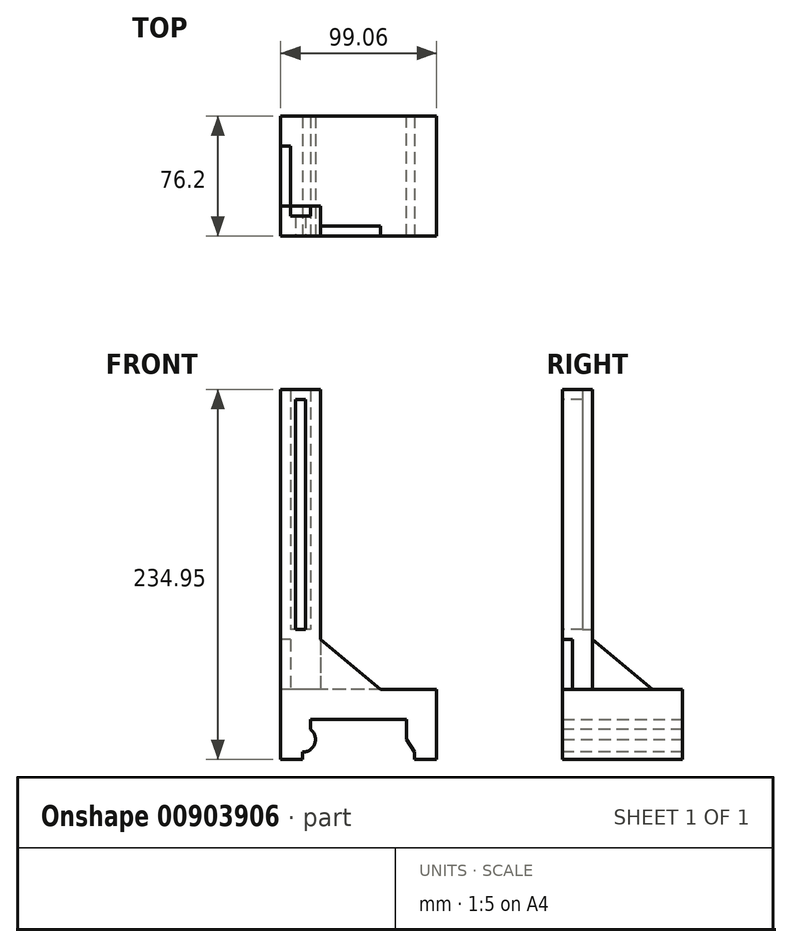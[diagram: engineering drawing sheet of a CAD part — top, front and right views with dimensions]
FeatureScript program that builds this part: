
annotation { "Feature Type Name" : "Feature", "Feature Type Description" : "" }
export const myFeature = defineFeature(function(context is Context, id is Id, definition is map)
    precondition{}
    {
        {
            var Q0;
            Q0=qCreatedBy(makeId("Front.planeOp"),FACE);
            var sketch = newSketch(context, id + "F0", { "sketchPlane" : qUnion([Q0])});
            skLineSegment(sketch, "E0.bottom", {"start": v(49.53, -22.23) * mm, "end": v(-49.53, -22.23) * mm});
            skLineSegment(sketch, "E0.top", {"start": v(49.53, 22.23) * mm, "end": v(-49.53, 22.23) * mm});
            skLineSegment(sketch, "E0.left", {"start": v(49.53, -22.23) * mm, "end": v(49.53, 22.23) * mm});
            skLineSegment(sketch, "E0.right", {"start": v(-49.53, -22.23) * mm, "end": v(-49.53, 22.22) * mm});
            skPoint(sketch, "E0.middle", {"position": v(0, 0) * mm});
            skLineSegment(sketch, "E1.bottom", {"start": v(30.48, -47.63) * mm, "end": v(-30.48, -47.63) * mm});
            skLineSegment(sketch, "E1.top", {"start": v(30.48, 3.18) * mm, "end": v(-30.48, 3.18) * mm});
            skLineSegment(sketch, "E1.left", {"start": v(30.48, -47.63) * mm, "end": v(30.48, 3.18) * mm});
            skLineSegment(sketch, "E1.right", {"start": v(-30.48, -47.63) * mm, "end": v(-30.48, 3.18) * mm});
            skPoint(sketch, "E1.middle", {"position": v(0, -22.23) * mm});
            skSolve(sketch);
        }
        {
            var Q0;
            Q0=makeQuery(id+"F0.imprint","IMPRINT",FACE,{"disambiguationData":[TD([[makeQuery(id+"F0.imprint","IMPRINT",EDGE,{"derivedFrom":sQuery(id+"F0.wireOp",EDGE,"E0.top")}),1.0]])]});
            extrude(context, id + "F1", {"entities" : qUnion([Q0]), "endBound" : BoundingType.SYMMETRIC, "depth" : 76.2 * mm, "offsetDistance" : 25.4 * mm});
        }
        {
            var Q0;
            Q0=qCreatedBy(makeId("Front.planeOp"),FACE);
            var sketch = newSketch(context, id + "F2", { "sketchPlane" : qUnion([Q0])});
            skLineSegment(sketch, "E2.bottom", {"start": v(35.56, -36.92) * mm, "end": v(-35.56, -36.92) * mm});
            skLineSegment(sketch, "E2.top", {"start": v(35.56, -9.52) * mm, "end": v(-35.56, -9.53) * mm});
            skLineSegment(sketch, "E2.left", {"start": v(35.56, -36.92) * mm, "end": v(35.56, -9.53) * mm});
            skLineSegment(sketch, "E2.right", {"start": v(-35.56, -36.92) * mm, "end": v(-35.56, -9.53) * mm});
            skPoint(sketch, "E2.middle", {"position": v(0, -23.22) * mm});
            skSolve(sketch);
        }
        {
            var Q0;
            Q0=makeQuery(id+"F2.imprint","IMPRINT",FACE,{"disambiguationData":[TD([[makeQuery(id+"F2.imprint","IMPRINT",EDGE,{"derivedFrom":sQuery(id+"F2.wireOp",EDGE,"E2.bottom")}),-1.0]])]});
            extrude(context, id + "F3", {"entities" : qUnion([Q0]), "operationType" : NewBodyOperationType.REMOVE, "endBound" : BoundingType.SYMMETRIC, "oppositeDirection" : true, "depth" : 101.6 * mm, "offsetDistance" : 25.4 * mm});
        }
        {
            var Q0;
            Q0=makeQuery(id+"F1.opExtrude","SWEPT_FACE",FACE,{"disambiguationData":[OSD([sQuery(id+"F0.wireOp",EDGE,"E0.top")])]});
            var sketch = newSketch(context, id + "F4", { "sketchPlane" : qUnion([Q0])});
            skPoint(sketch, "E3.right.end.orphan", {"position": v(-7.9, -5.96) * mm});
            skPoint(sketch, "E3.bottom.end.orphan", {"position": v(-7.9, -51.19) * mm});
            skLineSegment(sketch, "E4.bottom", {"start": v(-24.13, -38.1) * mm, "end": v(-49.53, -38.1) * mm});
            skLineSegment(sketch, "E4.top", {"start": v(-24.13, -19.05) * mm, "end": v(-49.53, -19.05) * mm});
            skLineSegment(sketch, "E4.left", {"start": v(-24.13, -38.1) * mm, "end": v(-24.13, -19.05) * mm});
            skLineSegment(sketch, "E4.right", {"start": v(-49.53, -38.1) * mm, "end": v(-49.53, -19.05) * mm});
            skPoint(sketch, "E4.middle", {"position": v(-36.83, -28.58) * mm});
            skSolve(sketch);
        }
        {
            var Q0;
            Q0=qSketchRegion(id+"F4",true);
            extrude(context, id + "F5", {"entities" : qUnion([Q0]), "operationType" : NewBodyOperationType.ADD, "depth" : 190.5 * mm, "offsetDistance" : 25.4 * mm});
        }
        {
            var Q0;
            Q0=makeQuery(id+"F5.opExtrude","SWEPT_FACE",FACE,{"disambiguationData":[OSD([sQuery(id+"F4.wireOp",EDGE,"E4.top")])]});
            var sketch = newSketch(context, id + "F6", { "sketchPlane" : qUnion([Q0])});
            skLineSegment(sketch, "E5.bottom", {"start": v(30.48, 212.73) * mm, "end": v(43.18, 212.73) * mm});
            skLineSegment(sketch, "E5.top", {"start": v(30.48, 60.33) * mm, "end": v(43.18, 60.33) * mm});
            skLineSegment(sketch, "E5.left", {"start": v(30.48, 212.73) * mm, "end": v(30.48, 60.33) * mm});
            skLineSegment(sketch, "E5.right", {"start": v(43.18, 212.73) * mm, "end": v(43.18, 60.33) * mm});
            skPoint(sketch, "E5.middle", {"position": v(36.83, 136.53) * mm});
            skSolve(sketch);
        }
        {
            var Q0;
            Q0=makeQuery(id+"F6.imprint","IMPRINT",FACE,{"disambiguationData":[TD([[makeQuery(id+"F6.imprint","IMPRINT",EDGE,{"derivedFrom":sQuery(id+"F6.wireOp",EDGE,"E5.bottom")}),-1.0]])]});
            extrude(context, id + "F7", {"entities" : qUnion([Q0]), "operationType" : NewBodyOperationType.REMOVE, "oppositeDirection" : true, "depth" : 6.35 * mm, "offsetDistance" : 25.4 * mm});
        }
        {
            var Q0;
            Q0=makeQuery(id+"F5.opExtrude","SWEPT_FACE",FACE,{"disambiguationData":[OSD([sQuery(id+"F4.wireOp",EDGE,"E4.top")])]});
            var sketch = newSketch(context, id + "F8", { "sketchPlane" : qUnion([Q0])});
            skLineSegment(sketch, "E6.bottom", {"start": v(33.65, 225.43) * mm, "end": v(20.96, 225.43) * mm});
            skLineSegment(sketch, "E6.top", {"start": v(33.66, 200.03) * mm, "end": v(20.96, 200.03) * mm});
            skLineSegment(sketch, "E6.left", {"start": v(33.65, 225.43) * mm, "end": v(33.66, 200.03) * mm});
            skLineSegment(sketch, "E6.right", {"start": v(20.96, 225.43) * mm, "end": v(20.96, 200.03) * mm});
            skPoint(sketch, "E6.middle", {"position": v(27.3, 212.73) * mm});
            skSolve(sketch);
        }
        {
            var Q0;
            {var subQ0=sQuery(id+"F8.wireOp",EDGE,"E6.bottom");Q0=makeQuery(id+"F8.imprint","IMPRINT",FACE,{"disambiguationData":[TD([[makeQuery(id+"F8.imprint","IMPRINT",EDGE,{"derivedFrom":subQ0}),1.0]])]});}
            var Q1;
            {var subQ0=sQuery(id+"F8.wireOp",EDGE,"E6.top");Q1=makeQuery(id+"F8.imprint","IMPRINT",FACE,{"disambiguationData":[TD([[makeQuery(id+"F8.imprint","IMPRINT",EDGE,{"derivedFrom":subQ0}),-1.0]])]});}
            var Q2;
            {var subQ1=makeQuery(id+"F7.boolean.opBoolean","COPY",EDGE,{"derivedFrom":makeQuery(id+"F7.opExtrude","CAP_EDGE",EDGE,{"disambiguationData":[OSD([sQuery(id+"F6.wireOp",EDGE,"E5.bottom")])],"isStart":true})});Q2=makeQuery(id+"F8.imprint","IMPRINT",FACE,{"disambiguationData":[TD([[makeQuery(id+"F8.imprint","IMPRINT",EDGE,{"derivedFrom":subQ1}),1.0]])]});}
            extrude(context, id + "F9", {"entities" : qUnion([Q0, Q1, Q2]), "operationType" : NewBodyOperationType.REMOVE, "oppositeDirection" : true, "depth" : 6.35 * mm, "offsetDistance" : 25.4 * mm});
        }
        {
            var Q0;
            Q0=makeQuery(id+"FqtUo2dF14dtISF_1.boolean.opBoolean","MERGE",FACE,{"derivedFrom":[makeQuery(id+"F1.opExtrude","CAP_FACE",FACE,{"disambiguationData":[OSD([sQuery(id+"F0.wireOp",EDGE,"E0.bottom"),sQuery(id+"F0.wireOp",EDGE,"E0.top"),sQuery(id+"F0.wireOp",EDGE,"E0.left"),sQuery(id+"F0.wireOp",EDGE,"E0.right"),sQuery(id+"F0.wireOp",EDGE,"E1.top"),sQuery(id+"F0.wireOp",EDGE,"E1.left"),sQuery(id+"F0.wireOp",EDGE,"E1.right")])],"isStart":false}),makeQuery(id+"FqtUo2dF14dtISF_1.opExtrude","CAP_FACE",FACE,{"disambiguationData":[OSD([sQuery(id+"Fa6pJ2o9r3T1tcu_1.wireOp",EDGE,"9ab49e5e-e781-4880-a481-f387394318e1.bottom"),sQuery(id+"Fa6pJ2o9r3T1tcu_1.wireOp",EDGE,"9ab49e5e-e781-4880-a481-f387394318e1.top"),sQuery(id+"Fa6pJ2o9r3T1tcu_1.wireOp",EDGE,"9ab49e5e-e781-4880-a481-f387394318e1.left"),sQuery(id+"Fa6pJ2o9r3T1tcu_1.wireOp",EDGE,"HMghRU8G-1H3M-OJ5W-wMgI-K1z1DDckNYTP"),sQuery(id+"Fa6pJ2o9r3T1tcu_1.wireOp",EDGE,"0KJWoq3j-ts2y-bZzM-44IR-2JegtjsgD1qJ")])],"isStart":true})]});
            var sketch = newSketch(context, id + "F10", { "sketchPlane" : qUnion([Q0])});
            skCircle(sketch, "E7", {"center": v(-35.56, -9.53) * mm, "radius": 8.06 * mm});
            skSolve(sketch);
        }
        {
            var Q0;
            Q0=qSketchRegion(id+"F10",true);
            extrude(context, id + "F11", {"entities" : qUnion([Q0]), "operationType" : NewBodyOperationType.ADD, "oppositeDirection" : true, "depth" : 76.2 * mm, "offsetDistance" : 25.4 * mm});
        }
        {
            var Q0;
            Q0=makeQuery(id+"F11.boolean.opBoolean","MERGE",FACE,{"derivedFrom":[makeQuery(id+"FqtUo2dF14dtISF_1.boolean.opBoolean","MERGE",FACE,{"derivedFrom":[makeQuery(id+"F1.opExtrude","CAP_FACE",FACE,{"disambiguationData":[OSD([sQuery(id+"F0.wireOp",EDGE,"E0.bottom"),sQuery(id+"F0.wireOp",EDGE,"E0.top"),sQuery(id+"F0.wireOp",EDGE,"E0.left"),sQuery(id+"F0.wireOp",EDGE,"E0.right"),sQuery(id+"F0.wireOp",EDGE,"E1.top"),sQuery(id+"F0.wireOp",EDGE,"E1.left"),sQuery(id+"F0.wireOp",EDGE,"E1.right")])],"isStart":false}),makeQuery(id+"FqtUo2dF14dtISF_1.opExtrude","CAP_FACE",FACE,{"disambiguationData":[OSD([sQuery(id+"Fa6pJ2o9r3T1tcu_1.wireOp",EDGE,"9ab49e5e-e781-4880-a481-f387394318e1.bottom"),sQuery(id+"Fa6pJ2o9r3T1tcu_1.wireOp",EDGE,"9ab49e5e-e781-4880-a481-f387394318e1.top"),sQuery(id+"Fa6pJ2o9r3T1tcu_1.wireOp",EDGE,"9ab49e5e-e781-4880-a481-f387394318e1.left"),sQuery(id+"Fa6pJ2o9r3T1tcu_1.wireOp",EDGE,"HMghRU8G-1H3M-OJ5W-wMgI-K1z1DDckNYTP"),sQuery(id+"Fa6pJ2o9r3T1tcu_1.wireOp",EDGE,"0KJWoq3j-ts2y-bZzM-44IR-2JegtjsgD1qJ")])],"isStart":true})]}),makeQuery(id+"F11.opExtrude","CAP_FACE",FACE,{"disambiguationData":[OSD([sQuery(id+"F10.wireOp",EDGE,"E7")])],"isStart":true})]});
            var sketch = newSketch(context, id + "F12", { "sketchPlane" : qUnion([Q0])});
            skLineSegment(sketch, "E8", {"start": v(35.56, -9.52) * mm, "end": v(35.56, -17.47) * mm});
            skLineSegment(sketch, "E9", {"start": v(35.56, -17.47) * mm, "end": v(30.48, -9.53) * mm});
            skLineSegment(sketch, "E10", {"start": v(30.48, -9.53) * mm, "end": v(35.56, -9.52) * mm});
            skSolve(sketch);
        }
        {
            var Q0;
            Q0=qSketchRegion(id+"F12",true);
            extrude(context, id + "F13", {"entities" : qUnion([Q0]), "operationType" : NewBodyOperationType.ADD, "oppositeDirection" : true, "depth" : 76.2 * mm, "offsetDistance" : 25.4 * mm});
        }
        {
            var Q0;
            Q0=makeQuery(id+"F13.boolean.opBoolean","MERGE",FACE,{"derivedFrom":[makeQuery(id+"F11.boolean.opBoolean","MERGE",FACE,{"derivedFrom":[makeQuery(id+"F5.boolean.opBoolean","MERGE",FACE,{"derivedFrom":[makeQuery(id+"F1.opExtrude","CAP_FACE",FACE,{"disambiguationData":[OSD([sQuery(id+"F0.wireOp",EDGE,"E0.bottom"),sQuery(id+"F0.wireOp",EDGE,"E0.top"),sQuery(id+"F0.wireOp",EDGE,"E0.left"),sQuery(id+"F0.wireOp",EDGE,"E0.right"),sQuery(id+"F0.wireOp",EDGE,"E1.top"),sQuery(id+"F0.wireOp",EDGE,"E1.left"),sQuery(id+"F0.wireOp",EDGE,"E1.right")])],"isStart":false}),makeQuery(id+"F5.opExtrude","SWEPT_FACE",FACE,{"disambiguationData":[OSD([sQuery(id+"F4.wireOp",EDGE,"E4.bottom")])]})]}),makeQuery(id+"F11.opExtrude","CAP_FACE",FACE,{"disambiguationData":[OSD([sQuery(id+"F10.wireOp",EDGE,"E7")])],"isStart":true})]}),makeQuery(id+"F13.opExtrude","CAP_FACE",FACE,{"disambiguationData":[OSD([sQuery(id+"F12.wireOp",EDGE,"E8"),sQuery(id+"F12.wireOp",EDGE,"E9"),sQuery(id+"F12.wireOp",EDGE,"E10")])],"isStart":true})]});
            var sketch = newSketch(context, id + "F14", { "sketchPlane" : qUnion([Q0])});
            skLineSegment(sketch, "E11", {"start": v(-24.13, 22.23) * mm, "end": v(13.97, 22.23) * mm});
            skLineSegment(sketch, "E12", {"start": v(-24.13, 22.23) * mm, "end": v(-24.13, 53.98) * mm});
            skLineSegment(sketch, "E13", {"start": v(-24.13, 53.98) * mm, "end": v(13.97, 22.23) * mm});
            skSolve(sketch);
        }
        {
            var Q0;
            Q0 = qSketchRegion(id + "F14", true);
            extrude(context, id + "F15", {"entities" : qUnion([Q0]), "operationType" : NewBodyOperationType.ADD, "oppositeDirection" : true, "depth" : 6.35 * mm, "offsetDistance" : 25.4 * mm});
        }
        {
            var Q0;
            Q0=makeQuery(id+"F5.boolean.opBoolean","MERGE",FACE,{"derivedFrom":[makeQuery(id+"F1.opExtrude","SWEPT_FACE",FACE,{"disambiguationData":[OSD([sQuery(id+"F0.wireOp",EDGE,"E0.right")])]}),makeQuery(id+"F5.opExtrude","SWEPT_FACE",FACE,{"disambiguationData":[OSD([sQuery(id+"F4.wireOp",EDGE,"E4.right")])]})]});
            var sketch = newSketch(context, id + "F16", { "sketchPlane" : qUnion([Q0])});
            skLineSegment(sketch, "E14", {"start": v(19.05, 22.23) * mm, "end": v(-19.05, 22.23) * mm});
            skLineSegment(sketch, "E15", {"start": v(19.05, 22.23) * mm, "end": v(19.05, 53.98) * mm});
            skLineSegment(sketch, "E16", {"start": v(19.05, 53.98) * mm, "end": v(-19.05, 22.22) * mm});
            skSolve(sketch);
        }
        {
            var Q0;
            Q0 = qSketchRegion(id + "F16", true);
            extrude(context, id + "F17", {"entities" : qUnion([Q0]), "operationType" : NewBodyOperationType.ADD, "oppositeDirection" : true, "depth" : 6.35 * mm, "offsetDistance" : 25.4 * mm});
        }
        {
            var Q0;
            Q0=makeQuery(id+"F15.boolean.opBoolean","MERGE",FACE,{"derivedFrom":[makeQuery(id+"F13.boolean.opBoolean","MERGE",FACE,{"derivedFrom":[makeQuery(id+"F11.boolean.opBoolean","MERGE",FACE,{"derivedFrom":[makeQuery(id+"F5.boolean.opBoolean","MERGE",FACE,{"derivedFrom":[makeQuery(id+"F1.opExtrude","CAP_FACE",FACE,{"disambiguationData":[OSD([sQuery(id+"F0.wireOp",EDGE,"E0.bottom"),sQuery(id+"F0.wireOp",EDGE,"E0.top"),sQuery(id+"F0.wireOp",EDGE,"E0.left"),sQuery(id+"F0.wireOp",EDGE,"E0.right"),sQuery(id+"F0.wireOp",EDGE,"E1.top"),sQuery(id+"F0.wireOp",EDGE,"E1.left"),sQuery(id+"F0.wireOp",EDGE,"E1.right")])],"isStart":false}),makeQuery(id+"F5.opExtrude","SWEPT_FACE",FACE,{"disambiguationData":[OSD([sQuery(id+"F4.wireOp",EDGE,"E4.bottom")])]})]}),makeQuery(id+"F11.opExtrude","CAP_FACE",FACE,{"disambiguationData":[OSD([sQuery(id+"F10.wireOp",EDGE,"E7")])],"isStart":true})]}),makeQuery(id+"F13.opExtrude","CAP_FACE",FACE,{"disambiguationData":[OSD([sQuery(id+"F12.wireOp",EDGE,"E8"),sQuery(id+"F12.wireOp",EDGE,"E9"),sQuery(id+"F12.wireOp",EDGE,"E10")])],"isStart":true})]}),makeQuery(id+"F15.opExtrude","CAP_FACE",FACE,{"disambiguationData":[OSD([sQuery(id+"F14.wireOp",EDGE,"E11"),sQuery(id+"F14.wireOp",EDGE,"E12"),sQuery(id+"F14.wireOp",EDGE,"E13")])],"isStart":true})]});
            var sketch = newSketch(context, id + "F18", { "sketchPlane" : qUnion([Q0])});
            skLineSegment(sketch, "E17.bottom", {"start": v(-40, 60.33) * mm, "end": v(-33.66, 60.33) * mm});
            skLineSegment(sketch, "E17.top", {"start": v(-40, 206.38) * mm, "end": v(-33.66, 206.38) * mm});
            skLineSegment(sketch, "E17.left", {"start": v(-40, 60.33) * mm, "end": v(-40, 206.38) * mm});
            skLineSegment(sketch, "E17.right", {"start": v(-33.66, 60.33) * mm, "end": v(-33.66, 206.38) * mm});
            skPoint(sketch, "E17.middle", {"position": v(-36.83, 133.35) * mm});
            skSolve(sketch);
        }
        {
            var Q0;
            Q0 = qSketchRegion(id + "F18", true);
            extrude(context, id + "F19", {"entities" : qUnion([Q0]), "operationType" : NewBodyOperationType.REMOVE, "oppositeDirection" : true, "depth" : 25.4 * mm, "offsetDistance" : 25.4 * mm});
        }
    });
